# Revit family: QF_MACOM_CH92C-N_G
name_source: partatom
category: Specialty Equipment
units: mm (PartAtom-declared; Revit-internal decimal feet)

## family parameters
Always vertical = Yes
Cut with Voids When Loaded = No
OmniClass Number = 23.40.40.14.17.14
OmniClass Title = Hot Plates
Part Type = Normal
Room Calculation Point = No
Round Connector Dimension = Use Diameter
Shared = No
Work Plane-Based = No

## types (2) — shared parameters
Capacity in Liters = 0,0 L
Cycle = 60 Hz
Default Elevation = 0,000 mm
Depth = 972,000 mm
Electric Connection Height = 284,000 mm
Gas Connection Height = 212,000 mm
Gas Pressure = 0,0 bar
Gas Size = 3/4"
Height = 985,000 mm
Manufacturer = MACOM
Phase = 1
Plate Depth = 737,000 mm
Plate Width = 445,000 mm
URL = https://www.acosmacom.com.br
Volts = 220 V
Volume = 0,85 m³
Watts = 100 W
Weight = 0,00 kg
Width = 900,000 mm

## per-type parameters (varying)
| type | Description | Gas Consumption GLP | Gas Consumption GN | Gas Input GLP | Gas Input GN |
| CH92C-N | CHAPA A GAS NATURAL 900HP MACOM COM MODULO BASE E PORTA - 900X972X900MM-900X972X900 |  | 1,9 m³/h | 0 Btu/h | 18000 Kcal/h |
| CH92C-G | CHAPA A GAS GLP 900HP MACOM COM MODULO BASE E PORTA - 900X972X900MM | 1,57 Kg/h | 0,0 m³/h | 71420 Btu/h |  |

note: column(s) folded — value = type name in every type: Model

## geometry (parser evidence)
native form markers: Sweep x3
no freeform markers — native parametric forms only
